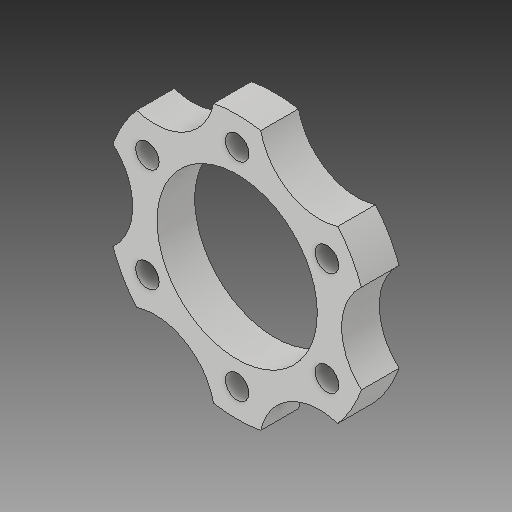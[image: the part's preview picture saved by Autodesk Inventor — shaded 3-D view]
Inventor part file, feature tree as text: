
AUTODESK INVENTOR PART (.ipt)
format: ipt  version: 2019.2 (Build 232265000, 265)  size: 148,992 bytes
history: native  units: mm
features: sketch x3, extrude x2, pattern_circular x2, hole x1
ambient origin geometry x8: Origin, YZ Plane, XZ Plane, XY Plane, X Axis, Y Axis, Z Axis, Center Point
bodies: Solid1 (feature_tree)
feature tree (8):
  extrude  "Extrusion1"  Depth=34.0mm
  hole  "Hole1"  [1 undecoded]
  pattern_circular  "Circular Pattern1"  Count=6 Angle=360.0deg
  extrude  "Extrusion2"  Depth=8.0mm TaperAngle=0.0deg
  pattern_circular  "Circular Pattern2"  Count=6 Angle=360.0deg
  sketch  "Sketch1"  dims[d0=22.0mm d1=34.0mm]
  sketch  "Sketch2"  dims[d2=8.0mm d3=0.0mm d4=22.0mm]
  sketch  "Sketch3"  dims[d5=5.0mm d6=10.0mm d7=3.023mm d8=2.0mm d9=14.3117mm d10=8.0mm d11=20.594885mm d12=60.0mm d13=360.0deg d15=8.0mm d16=0.0mm d17=60.0mm d18=360.0deg d20=56.0mm]
note: 1 required parameter value undecoded (feature->parameter linkage not recoverable at this tier; creation-order binding heuristic only, values carry confidence <= 0.55)
